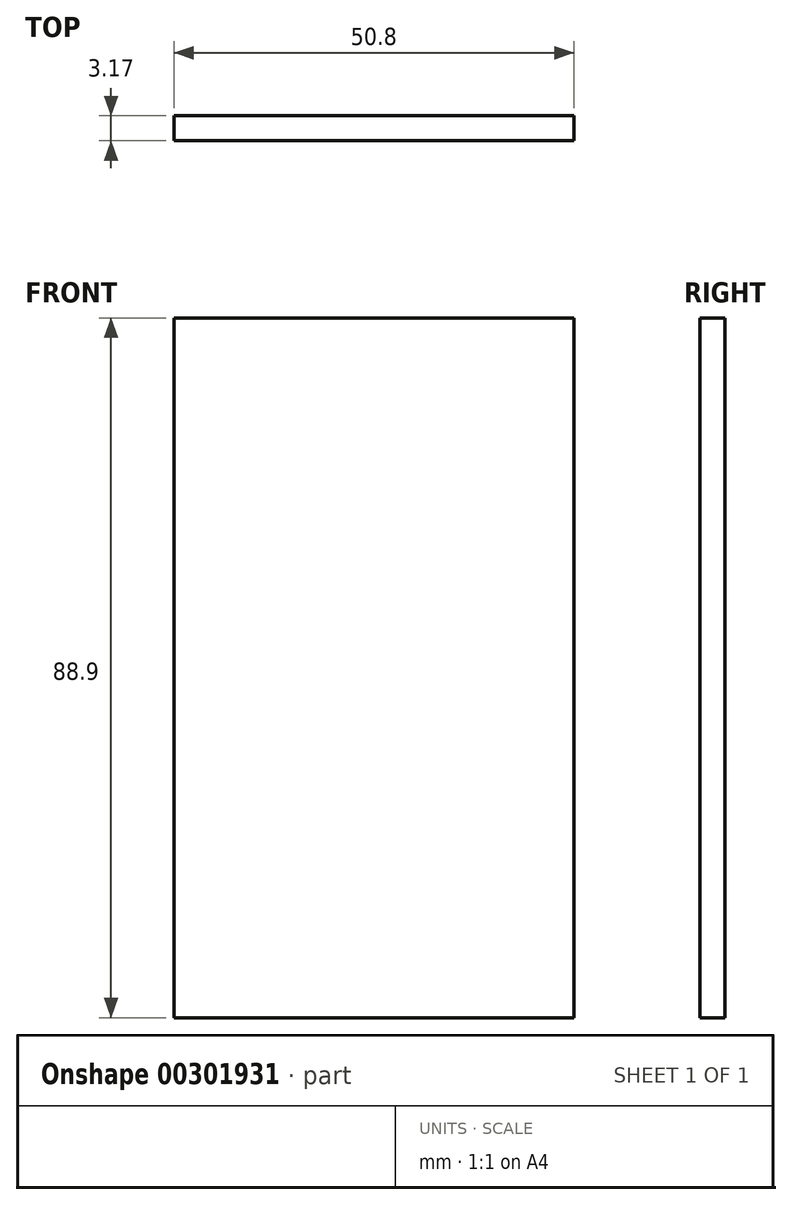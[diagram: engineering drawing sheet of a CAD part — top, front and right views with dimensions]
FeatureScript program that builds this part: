
annotation { "Feature Type Name" : "Feature", "Feature Type Description" : "" }
export const myFeature = defineFeature(function(context is Context, id is Id, definition is map)
    precondition{}
    {
        {
            var Q0;
            Q0=qCreatedBy(makeId("Front.planeOp"),FACE);
            var sketch = newSketch(context, id + "F0", { "sketchPlane" : qUnion([Q0])});
            skLineSegment(sketch, "E0.bottom", {"start": v(-25.4, 44.45) * mm, "end": v(25.4, 44.45) * mm});
            skLineSegment(sketch, "E0.top", {"start": v(-25.4, -44.45) * mm, "end": v(25.4, -44.45) * mm});
            skLineSegment(sketch, "E0.left", {"start": v(-25.4, 44.45) * mm, "end": v(-25.4, -44.45) * mm});
            skLineSegment(sketch, "E0.right", {"start": v(25.4, 44.45) * mm, "end": v(25.4, -44.45) * mm});
            skPoint(sketch, "E0.middle", {"position": v(0, 0) * mm});
            skSolve(sketch);
        }
        {
            var Q0;
            Q0=makeQuery(id+"F0.imprint","IMPRINT",FACE,{"disambiguationData":[TD([[makeQuery(id+"F0.imprint","IMPRINT",EDGE,{"derivedFrom":sQuery(id+"F0.wireOp",EDGE,"E0.bottom")}),-1.0]])]});
            extrude(context, id + "F1", {"entities" : qUnion([Q0]), "depth" : 3.17 * mm});
        }
    });
